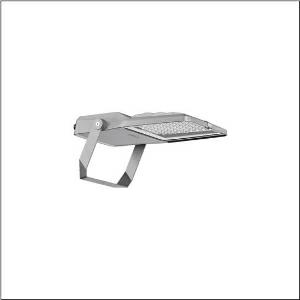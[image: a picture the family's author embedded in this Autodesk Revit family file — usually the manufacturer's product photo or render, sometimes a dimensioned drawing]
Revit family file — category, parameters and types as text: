
# Revit family: floodlight_fl_21_iq_mini___pl33t_5xa7772d3f1a_bc4e
name_source: partatom
category: Lighting Fixtures
units: mm (PartAtom-declared; Revit-internal decimal feet)

## family parameters
Cut with Voids When Loaded = No
Host = Face
Light Source = No
Part Type = Normal
Room Calculation Point = No
Round Connector Dimension = Use Diameter
Shared = No

## types (1)
- --- (1 x LED, 15160 lm, 143 W, 3000K)
    Apparent Load = 143 VA
    CIE Flux Codes = 26 75 99 100 100
    Color Rendering = 80
    Color Temperature = 3000K
    Default Elevation = 1800 mm
    Description = Floodlight FL 21 iQ mini, floodlight, primary light control with lens, of PMMA, primary optical cover: protective disc, of toughened safety glass, transparent, light distribution: PL33T, light emission: direct distribution, installation type: surface-mounted, LED, High Power LED, rated luminous flux: 15.160lm, luminous efficacy: 106lm/W, light colour: 830, colour temperature: 3000K, control gear: iQ Street-Remote/DALI, control: Street-Remote, Auto-Match, Temp-Guard, Night-Set, Smart-Wire, Desk-Remote (wireless, voltage-free reading and setting of iQ features in the workshop via application-optimized NFC function/RFID function), optimised constant luminous flux control (CLO 2.0), with terminal, 6-pole, mains connection: 220..240V, AC, 50/60Hz, start of lifetime: 143W, end of service life: 152W, reduction: 61W, luminaire housing, of diecast aluminium, powder-coated, Siteco® metallic grey (DB 702S), corrosivity category C5 mid according to DIN EN ISO 12944, suitable for swimming pools, chlorine-resistant, sealing non-destructively replaceable, mounting bracket, of steel, galvanised, powder-coated, Siteco® metallic grey (DB 702S), protection rating (complete): IP66, insulation class (complete): insulation class II (safety insulation), certification: CE, ENEC, VDE, protection symbol: D, impact resistance: IK08, permissible operating ambient temperature: -40..+40°C, permissible operating ambient temperature for outdoor applications: -40..+50°C, standard: DIN EN 12944, LABS conformity tested according to VDMA 24364:2018-05, packaging unit: 1 piece

Light Distribution: PL33T
    Height = 70 mm
    Lamp = 1 x LED
    Lamp Light Flux = 15160 lm
    Lamp Power = 143 W
    Lamp count = 1
    Length = 485 mm
    Luminous efficacy = 106 lm/W
    Manufacturer = Siteco
    ModVariant = No
    Model = 5XA7772D3F1A
    Number of Poles = 1
    OnlyDefault = Yes
    Power Factor = 1
    Product Name = Floodlight FL 21 iQ mini | PL33T
    Product group = floodlight | pylon annexe
    ProductGroupID = 6200
    Protection Class = Protection class II
    Protection Degree = IP 66
    RLX_Detail_Level = 1
    RLX_Emergency_Light_Flux = 0 lm
    RLX_Emergency_Type = 0
    RLX_Emergency_Type_DB = No
    RlxData = <blob elided: 96361 chars, md5=338339dd>
    Socket = socket
    Standby Power = 0 W
    System Light Flux = 15160 lm
    System Power = 143 W
    Type Comments = factory setting: luminous flux: 100 % | dim-lin: 254 | 730 mA
    Type Image = l_1006845.jpg
    URL = http://relux.com
    VarID = @adj_148894
    Voltage = 0 V
    Weight = 0.00 kg
    Width = 337 mm

## geometry (parser evidence)
native form markers: Blend x4, Sweep x13
no freeform markers — native parametric forms only
